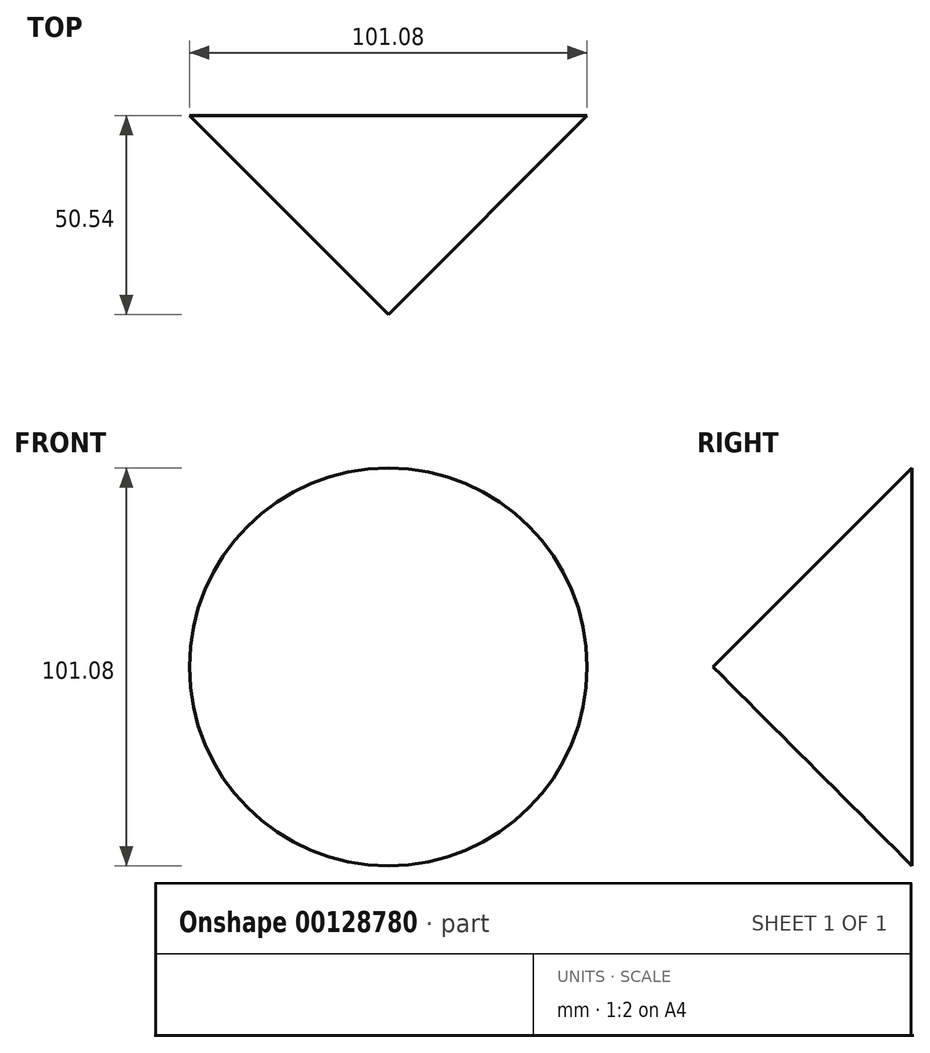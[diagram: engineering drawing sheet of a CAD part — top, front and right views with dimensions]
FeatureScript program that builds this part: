
annotation { "Feature Type Name" : "Feature", "Feature Type Description" : "" }
export const myFeature = defineFeature(function(context is Context, id is Id, definition is map)
    precondition{}
    {
        {
            var Q0;
            Q0=qCreatedBy(makeId("Front.planeOp"),FACE);
            var sketch = newSketch(context, id + "F0", { "sketchPlane" : qUnion([Q0])});
            skCircle(sketch, "E0", {"center": v(0, 0) * mm, "radius": 50.54 * mm});
            skSolve(sketch);
        }
        {
            var Q0;
            Q0 = qSketchRegion(id + "F0", true);
            extrude(context, id + "F1", {"entities" : qUnion([Q0]), "depth" : 254 * mm, "hasDraft" : true, "draftAngle" : 45 * degree, "draftPullDirection" : true});
        }
    });
